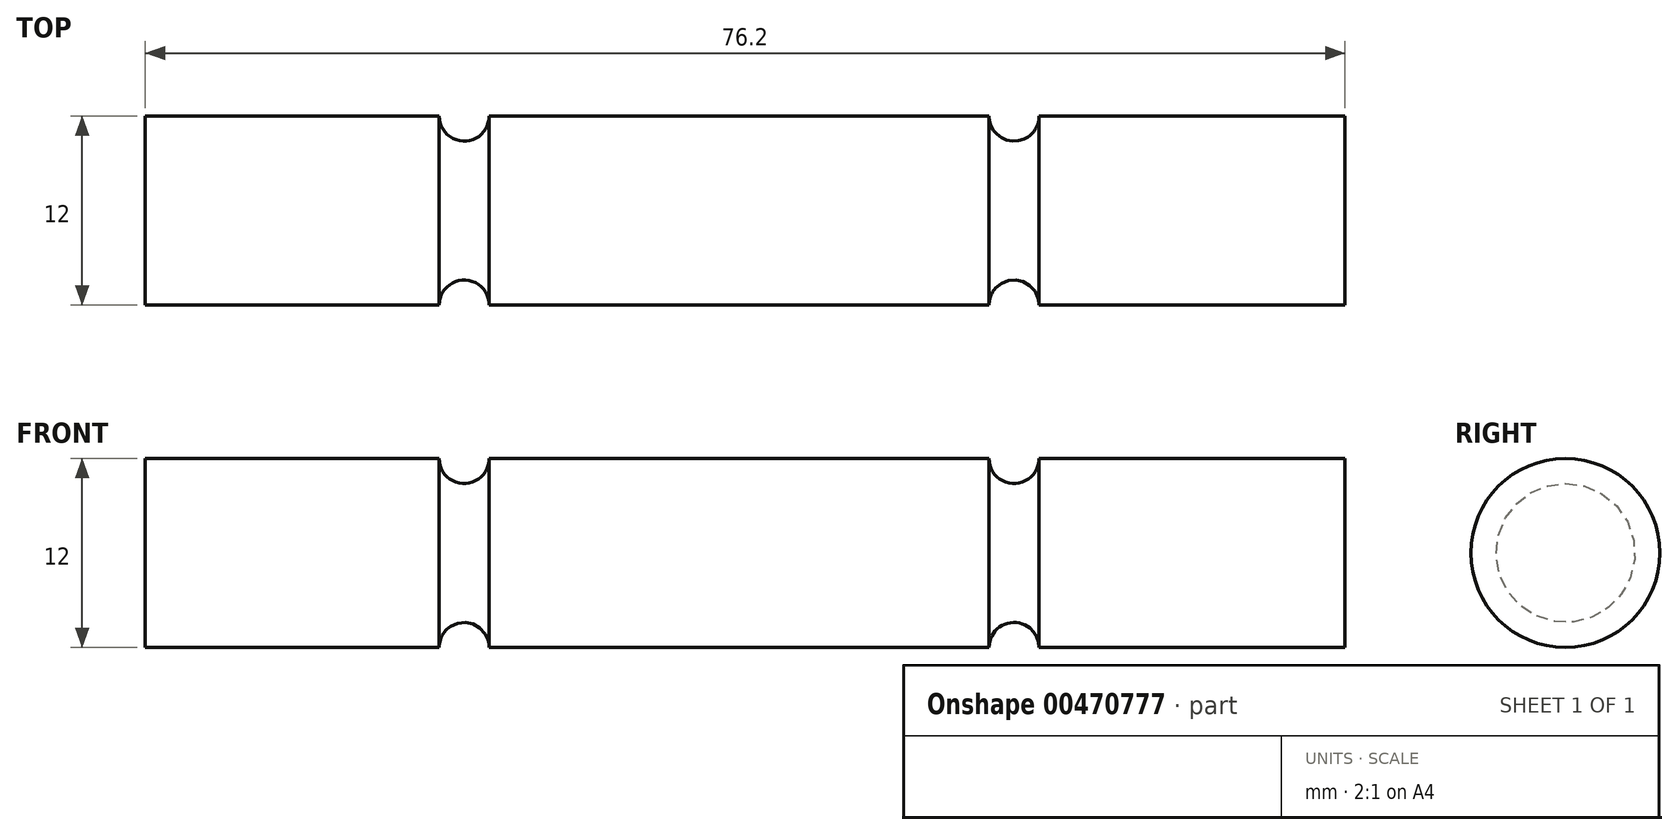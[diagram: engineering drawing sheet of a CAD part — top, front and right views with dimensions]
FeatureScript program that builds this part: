
annotation { "Feature Type Name" : "Feature", "Feature Type Description" : "" }
export const myFeature = defineFeature(function(context is Context, id is Id, definition is map)
    precondition{}
    {
        {
            var Q0;
            Q0=qCreatedBy(makeId("Top.planeOp"),FACE);
            var sketch = newSketch(context, id + "F0", { "sketchPlane" : qUnion([Q0])});
            skLineSegment(sketch, "E0.bottom", {"start": v(0, 0) * mm, "end": v(76.2, 0) * mm});
            skLineSegment(sketch, "E0.top", {"start": v(0, 6) * mm, "end": v(18.67, 6) * mm});
            skLineSegment(sketch, "E0.left", {"start": v(0, 0) * mm, "end": v(0, 6) * mm});
            skLineSegment(sketch, "E0.right", {"start": v(76.2, 0) * mm, "end": v(76.2, 6) * mm});
            skLineSegment(sketch, "E1", {"start": v(21.84, 0) * mm, "end": v(21.84, 6) * mm, "construction": true});
            skLineSegment(sketch, "E2", {"start": v(53.6, 0) * mm, "end": v(53.6, 6) * mm, "construction": true});
            skLineSegment(sketch, "E3", {"start": v(18.67, 6) * mm, "end": v(18.67, 0) * mm, "construction": true});
            skLineSegment(sketch, "E4", {"start": v(56.77, 6) * mm, "end": v(56.77, 0) * mm, "construction": true});
            skLineSegment(sketch, "E5.trimOffspring", {"start": v(21.84, 6) * mm, "end": v(53.6, 6) * mm});
            skLineSegment(sketch, "E6.trimOffspring", {"start": v(56.77, 6) * mm, "end": v(76.2, 6) * mm});
            skArc(sketch, "E7", {"start": v(18.67, 6) * mm, "mid": v(20.26, 4.41) * mm, "end": v(21.84, 6) * mm});
            skArc(sketch, "E8", {"start": v(53.6, 6) * mm, "mid": v(55.18, 4.41) * mm, "end": v(56.77, 6) * mm});
            skText(sketch, "E9", { "text": "M12x1.5\n", "fontName": "OpenSans-Regular.ttf"});
            skText(sketch, "E10", { "text": "M12x1.25\n", "fontName": "OpenSans-Regular.ttf"});
            const initialGuessF0  = {"E9": [-0.01467, 0.01012, 1, 0, 0.00277], "E10": [0.05565, 0.01126, 1, 0, 0.00368]};
            skSetInitialGuess(sketch, initialGuessF0);
            skSolve(sketch);
        }
        {
            var Q0;
            Q0=makeQuery(id+"F0.imprint","IMPRINT",FACE,{"disambiguationData":[TD([[makeQuery(id+"F0.imprint","IMPRINT",EDGE,{"derivedFrom":sQuery(id+"F0.wireOp",EDGE,"E0.bottom")}),1.0]])]});
            var Q1;
            Q1=sQuery(id+"F0.wireOp",EDGE,"E0.bottom");
            revolve(context, id + "F1", {"entities" : qUnion([Q0]), "axis" : qUnion([Q1]), "revolveType" : RevolveType.FULL});
        }
    });
